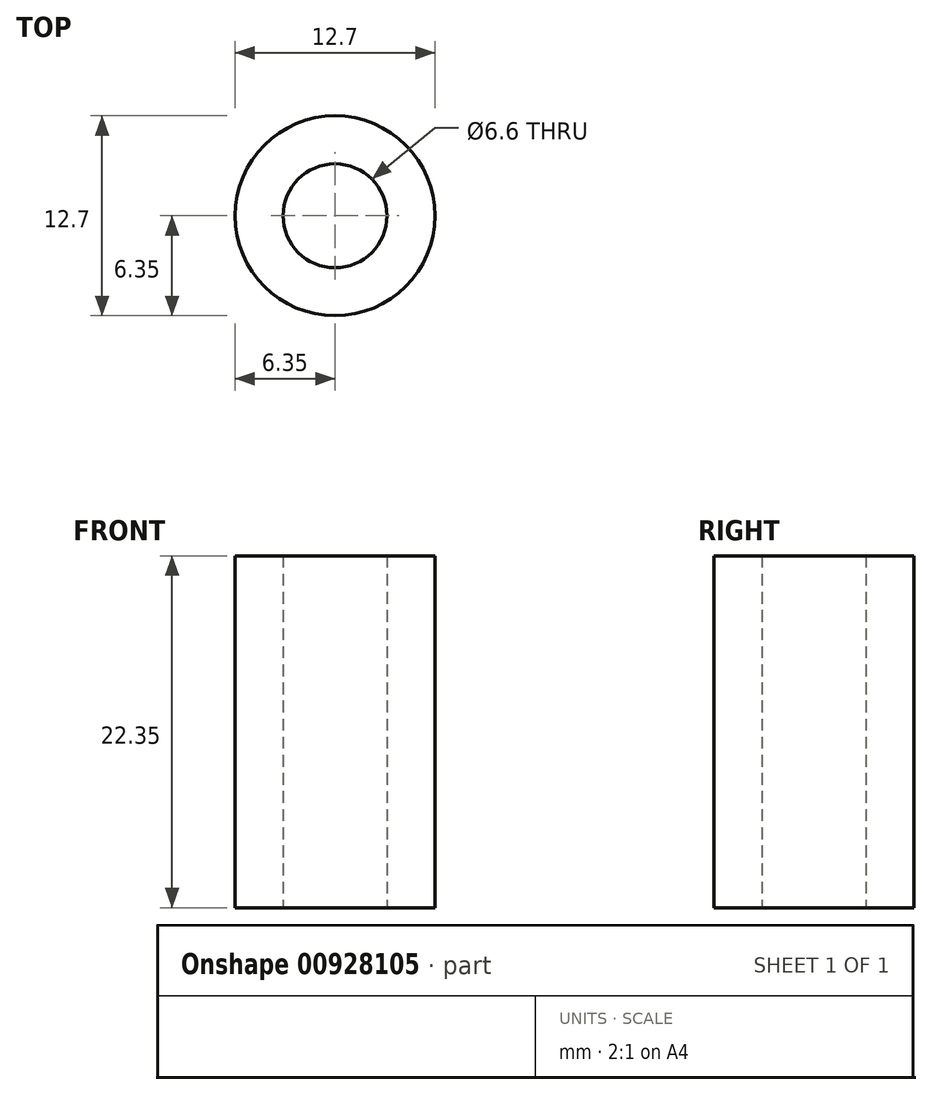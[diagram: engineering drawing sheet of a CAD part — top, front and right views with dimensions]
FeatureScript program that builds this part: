
annotation { "Feature Type Name" : "Feature", "Feature Type Description" : "" }
export const myFeature = defineFeature(function(context is Context, id is Id, definition is map)
    precondition{}
    {
        {
            var Q0;
            Q0=qCreatedBy(makeId("Top.planeOp"),FACE);
            var sketch = newSketch(context, id + "F0", { "sketchPlane" : qUnion([Q0])});
            skCircle(sketch, "E0", {"center": v(0, 0) * mm, "radius": 6.35 * mm});
            skCircle(sketch, "E1", {"center": v(0, 0) * mm, "radius": 3.3 * mm});
            skSolve(sketch);
        }
        {
            var Q0;
            Q0=qSketchRegion(id+"F0",true);
            extrude(context, id + "F1", {"entities" : qUnion([Q0]), "depth" : 22.35 * mm, "offsetDistance" : 25.4 * mm});
        }
    });
